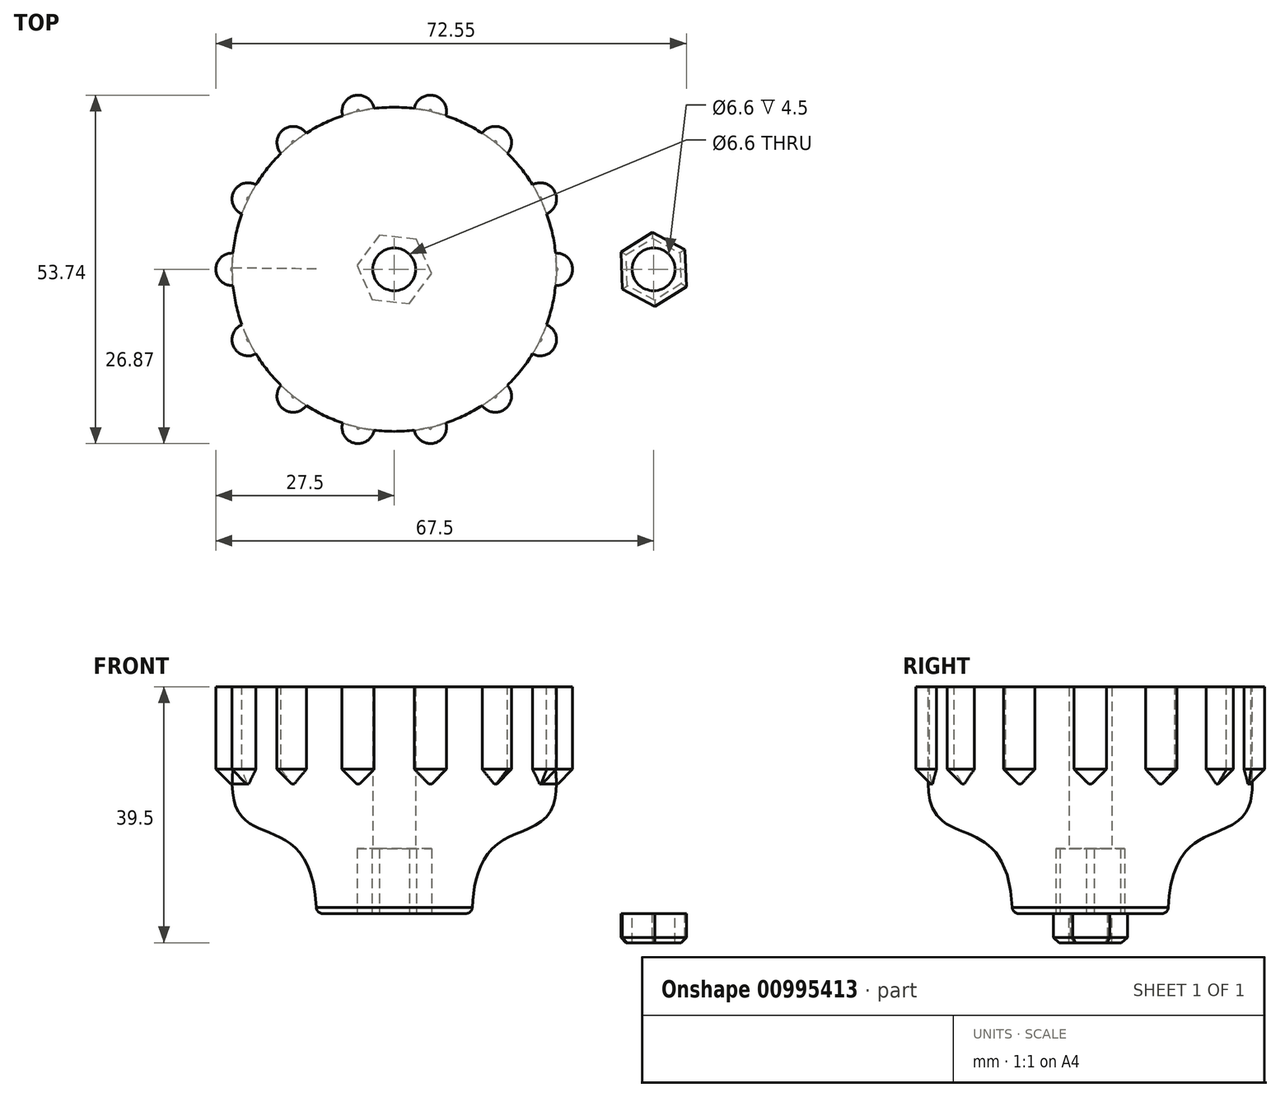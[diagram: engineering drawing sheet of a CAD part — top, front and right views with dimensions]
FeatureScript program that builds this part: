
annotation { "Feature Type Name" : "Feature", "Feature Type Description" : "" }
export const myFeature = defineFeature(function(context is Context, id is Id, definition is map)
    precondition{}
    {
        {
            var Q0;
            Q0=qCreatedBy(makeId("Front.planeOp"),FACE);
            var sketch = newSketch(context, id + "F0", { "sketchPlane" : qUnion([Q0])});
            skLineSegment(sketch, "E0", {"start": v(0, 60.16) * mm, "end": v(0, -58.96) * mm, "construction": true});
            skLineSegment(sketch, "E1", {"start": v(0, -19.71) * mm, "end": v(-12, -19.71) * mm});
            skLineSegment(sketch, "E2", {"start": v(0, 15.29) * mm, "end": v(-25, 15.29) * mm});
            skLineSegment(sketch, "E3", {"start": v(-25, 15.29) * mm, "end": v(-25, 0.29) * mm});
            skFitSpline(sketch, "E4", {"points": [v(-25, 0.29) * mm, v(-12, -19.71) * mm], "startDerivative": vector(0, -34.44) * mm, "endDerivative": vector(1.05, -52.25) * mm});
            skLineSegment(sketch, "E5", {"start": v(0, -19.71) * mm, "end": v(0, 15.29) * mm});
            skSolve(sketch);
        }
        {
            var Q0;
            Q0 = qSketchRegion(id + "F0", true);
            var Q1;
            Q1=sQuery(id+"F0.wireOp",EDGE,"E0");
            revolve(context, id + "F1", {"surfaceOperationType" : NewSurfaceOperationType.NEW, "entities" : qUnion([Q0]), "axis" : qUnion([Q1]), "revolveType" : RevolveType.FULL});
        }
        {
            var Q0;
            Q0=makeQuery(id+"F1.opRevolve","SWEPT_FACE",FACE,{"disambiguationData":[OSD([sQuery(id+"F0.wireOp",EDGE,"E1")])]});
            var sketch = newSketch(context, id + "F2", { "sketchPlane" : qUnion([Q0])});
            skCircle(sketch, "E6", {"center": v(0, 0) * mm, "radius": 3.3 * mm});
            skSolve(sketch);
        }
        {
            var Q0;
            Q0 = qSketchRegion(id + "F2", true);
            extrude(context, id + "F3", {"entities" : qUnion([Q0]), "operationType" : NewBodyOperationType.REMOVE, "endBound" : BoundingType.UP_TO_NEXT, "oppositeDirection" : true, "depth" : 25 * mm, "offsetDistance" : 25 * mm});
        }
        {
            var Q0;
            Q0=makeQuery(id+"F1.opRevolve","SWEPT_FACE",FACE,{"disambiguationData":[OSD([sQuery(id+"F0.wireOp",EDGE,"E1")])]});
            var sketch = newSketch(context, id + "F4", { "sketchPlane" : qUnion([Q0])});
            skCircle(sketch, "E7.cCircle", {"center": v(0, 0) * mm, "radius": 5 * mm, "construction": true});
            skLineSegment(sketch, "E7.0", {"start": v(5.74, 0.63) * mm, "end": v(3.42, -4.65) * mm});
            skLineSegment(sketch, "E7.1", {"start": v(3.42, -4.65) * mm, "end": v(-2.32, -5.29) * mm});
            skLineSegment(sketch, "E7.2", {"start": v(-2.32, -5.29) * mm, "end": v(-5.74, -0.63) * mm});
            skLineSegment(sketch, "E7.3", {"start": v(-5.74, -0.63) * mm, "end": v(-3.42, 4.65) * mm});
            skLineSegment(sketch, "E7.4", {"start": v(-3.42, 4.65) * mm, "end": v(2.32, 5.29) * mm});
            skLineSegment(sketch, "E7.5", {"start": v(2.32, 5.29) * mm, "end": v(5.74, 0.63) * mm});
            skPoint(sketch, "E7.0.midPoint", {"position": v(4.58, -2.01) * mm});
            skSolve(sketch);
        }
        {
            var Q0;
            Q0 = qSketchRegion(id + "F4", true);
            extrude(context, id + "F5", {"entities" : qUnion([Q0]), "operationType" : NewBodyOperationType.REMOVE, "oppositeDirection" : true, "depth" : 10 * mm, "offsetDistance" : 25 * mm});
        }
        {
            var Q0;
            Q0=makeQuery(id+"F1.opRevolve","SWEPT_FACE",FACE,{"disambiguationData":[OSD([sQuery(id+"F0.wireOp",EDGE,"E2")])]});
            var sketch = newSketch(context, id + "F6", { "sketchPlane" : qUnion([Q0])});
            skArc(sketch, "E8", {"start": v(-24.87, 2.5) * mm, "mid": v(-27.5, 0) * mm, "end": v(-24.88, -2.5) * mm});
            skArc(sketch, "E9", {"start": v(-24.88, 2.5) * mm, "mid": v(-25, 0) * mm, "end": v(-24.88, -2.5) * mm});
            skArc(sketch, "E10.1.0", {"start": v(-23.5, -8.54) * mm, "mid": v(-24.78, -11.93) * mm, "end": v(-21.33, -13.04) * mm});
            skArc(sketch, "E10.1.1", {"start": v(-23.5, -8.54) * mm, "mid": v(-22.52, -10.85) * mm, "end": v(-21.33, -13.04) * mm});
            skArc(sketch, "E10.2.0", {"start": v(-17.46, -17.9) * mm, "mid": v(-17.15, -21.5) * mm, "end": v(-13.56, -21) * mm});
            skArc(sketch, "E10.2.1", {"start": v(-17.46, -17.9) * mm, "mid": v(-15.59, -19.55) * mm, "end": v(-13.56, -21) * mm});
            skArc(sketch, "E10.3.0", {"start": v(-7.97, -23.7) * mm, "mid": v(-6.12, -26.81) * mm, "end": v(-3.1, -24.8) * mm});
            skArc(sketch, "E10.3.1", {"start": v(-7.97, -23.7) * mm, "mid": v(-5.56, -24.37) * mm, "end": v(-3.1, -24.8) * mm});
            skArc(sketch, "E10.4.0", {"start": v(3.1, -24.8) * mm, "mid": v(6.12, -26.81) * mm, "end": v(7.97, -23.7) * mm});
            skArc(sketch, "E10.4.1", {"start": v(3.1, -24.8) * mm, "mid": v(5.56, -24.37) * mm, "end": v(7.97, -23.7) * mm});
            skArc(sketch, "E10.5.0", {"start": v(13.56, -21) * mm, "mid": v(17.15, -21.5) * mm, "end": v(17.46, -17.9) * mm});
            skArc(sketch, "E10.5.1", {"start": v(13.56, -21) * mm, "mid": v(15.59, -19.55) * mm, "end": v(17.46, -17.9) * mm});
            skArc(sketch, "E10.6.0", {"start": v(21.33, -13.04) * mm, "mid": v(24.78, -11.93) * mm, "end": v(23.5, -8.54) * mm});
            skArc(sketch, "E10.6.1", {"start": v(21.33, -13.04) * mm, "mid": v(22.52, -10.85) * mm, "end": v(23.5, -8.54) * mm});
            skArc(sketch, "E10.7.0", {"start": v(24.87, -2.5) * mm, "mid": v(27.5, 0) * mm, "end": v(24.88, 2.5) * mm});
            skArc(sketch, "E10.7.1", {"start": v(24.88, -2.5) * mm, "mid": v(25, 0) * mm, "end": v(24.88, 2.5) * mm});
            skArc(sketch, "E10.8.0", {"start": v(23.5, 8.54) * mm, "mid": v(24.78, 11.93) * mm, "end": v(21.33, 13.04) * mm});
            skArc(sketch, "E10.8.1", {"start": v(23.5, 8.54) * mm, "mid": v(22.52, 10.85) * mm, "end": v(21.33, 13.04) * mm});
            skArc(sketch, "E10.9.0", {"start": v(17.46, 17.9) * mm, "mid": v(17.15, 21.5) * mm, "end": v(13.56, 21) * mm});
            skArc(sketch, "E10.9.1", {"start": v(17.46, 17.9) * mm, "mid": v(15.59, 19.55) * mm, "end": v(13.56, 21) * mm});
            skArc(sketch, "E10.10.0", {"start": v(7.97, 23.7) * mm, "mid": v(6.12, 26.81) * mm, "end": v(3.1, 24.8) * mm});
            skArc(sketch, "E10.10.1", {"start": v(7.97, 23.7) * mm, "mid": v(5.56, 24.37) * mm, "end": v(3.1, 24.8) * mm});
            skArc(sketch, "E10.11.0", {"start": v(-3.1, 24.8) * mm, "mid": v(-6.12, 26.81) * mm, "end": v(-7.97, 23.7) * mm});
            skArc(sketch, "E10.11.1", {"start": v(-3.1, 24.8) * mm, "mid": v(-5.56, 24.37) * mm, "end": v(-7.97, 23.7) * mm});
            skArc(sketch, "E10.12.0", {"start": v(-13.56, 21) * mm, "mid": v(-17.15, 21.5) * mm, "end": v(-17.46, 17.9) * mm});
            skArc(sketch, "E10.12.1", {"start": v(-13.56, 21) * mm, "mid": v(-15.59, 19.55) * mm, "end": v(-17.46, 17.9) * mm});
            skArc(sketch, "E10.13.0", {"start": v(-21.33, 13.04) * mm, "mid": v(-24.78, 11.93) * mm, "end": v(-23.5, 8.54) * mm});
            skArc(sketch, "E10.13.1", {"start": v(-21.33, 13.04) * mm, "mid": v(-22.52, 10.85) * mm, "end": v(-23.5, 8.54) * mm});
            skSolve(sketch);
        }
        {
            var Q0;
            Q0 = qSketchRegion(id + "F6", true);
            extrude(context, id + "F7", {"entities" : qUnion([Q0]), "operationType" : NewBodyOperationType.ADD, "oppositeDirection" : true, "depth" : 15 * mm, "offsetDistance" : 25 * mm});
        }
        {
            var Q0;
            Q0=makeQuery(id+"F7.opExtrude","CAP_EDGE",EDGE,{"disambiguationData":[OSD([sQuery(id+"F6.wireOp",EDGE,"E8")])],"isStart":false});
            var Q1;
            Q1=makeQuery(id+"F7.opExtrude","CAP_EDGE",EDGE,{"disambiguationData":[OSD([sQuery(id+"F6.wireOp",EDGE,"E10.13.0")])],"isStart":false});
            var Q2;
            Q2=makeQuery(id+"F7.opExtrude","CAP_EDGE",EDGE,{"disambiguationData":[OSD([sQuery(id+"F6.wireOp",EDGE,"E10.12.0")])],"isStart":false});
            var Q3;
            Q3=makeQuery(id+"F7.opExtrude","CAP_EDGE",EDGE,{"disambiguationData":[OSD([sQuery(id+"F6.wireOp",EDGE,"E10.11.0")])],"isStart":false});
            var Q4;
            Q4=makeQuery(id+"F7.opExtrude","CAP_EDGE",EDGE,{"disambiguationData":[OSD([sQuery(id+"F6.wireOp",EDGE,"E10.10.0")])],"isStart":false});
            var Q5;
            Q5=makeQuery(id+"F7.opExtrude","CAP_EDGE",EDGE,{"disambiguationData":[OSD([sQuery(id+"F6.wireOp",EDGE,"E10.9.0")])],"isStart":false});
            var Q6;
            Q6=makeQuery(id+"F7.opExtrude","CAP_EDGE",EDGE,{"disambiguationData":[OSD([sQuery(id+"F6.wireOp",EDGE,"E10.8.0")])],"isStart":false});
            var Q7;
            Q7=makeQuery(id+"F7.opExtrude","CAP_EDGE",EDGE,{"disambiguationData":[OSD([sQuery(id+"F6.wireOp",EDGE,"E10.7.0")])],"isStart":false});
            var Q8;
            Q8=makeQuery(id+"F7.opExtrude","CAP_EDGE",EDGE,{"disambiguationData":[OSD([sQuery(id+"F6.wireOp",EDGE,"E10.6.0")])],"isStart":false});
            var Q9;
            Q9=makeQuery(id+"F7.opExtrude","CAP_EDGE",EDGE,{"disambiguationData":[OSD([sQuery(id+"F6.wireOp",EDGE,"E10.5.0")])],"isStart":false});
            var Q10;
            Q10=makeQuery(id+"F7.opExtrude","CAP_EDGE",EDGE,{"disambiguationData":[OSD([sQuery(id+"F6.wireOp",EDGE,"E10.4.0")])],"isStart":false});
            var Q11;
            Q11=makeQuery(id+"F7.opExtrude","CAP_EDGE",EDGE,{"disambiguationData":[OSD([sQuery(id+"F6.wireOp",EDGE,"E10.3.0")])],"isStart":false});
            var Q12;
            Q12=makeQuery(id+"F7.opExtrude","CAP_EDGE",EDGE,{"disambiguationData":[OSD([sQuery(id+"F6.wireOp",EDGE,"E10.2.0")])],"isStart":false});
            var Q13;
            Q13=makeQuery(id+"F7.opExtrude","CAP_EDGE",EDGE,{"disambiguationData":[OSD([sQuery(id+"F6.wireOp",EDGE,"E10.1.0")])],"isStart":false});
            chamfer(context, id + "F8", {"entities" : qUnion([Q0, Q1, Q2, Q3, Q4, Q5, Q6, Q7, Q8, Q9, Q10, Q11, Q12, Q13]), "width" : 2.25 * mm, "tangentPropagation" : true});
        }
        {
            var Q0;
            Q0=makeQuery(id+"F1.opRevolve","SWEPT_EDGE",EDGE,{"disambiguationData":[OSD([sQuery(id+"F0.wireOp",EDGE,"E1"),sQuery(id+"F0.wireOp",EDGE,"E4")])]});
            fillet(context, id + "F9", {"entities" : qUnion([Q0]), "radius" : 1 * mm, "tangentPropagation" : true, "allowEdgeOverflow" : false});
        }
        {
            var Q0;
            Q0=makeQuery(id+"F1.opRevolve","SWEPT_FACE",FACE,{"disambiguationData":[OSD([sQuery(id+"F0.wireOp",EDGE,"E1")])]});
            var sketch = newSketch(context, id + "F10", { "sketchPlane" : qUnion([Q0])});
            skCircle(sketch, "E11.cCircle", {"center": v(40, 0) * mm, "radius": 4.95 * mm, "construction": true});
            skLineSegment(sketch, "E11.0", {"start": v(35.15, 3.03) * mm, "end": v(40.2, 5.71) * mm});
            skLineSegment(sketch, "E11.1", {"start": v(40.2, 5.71) * mm, "end": v(45.05, 2.68) * mm});
            skLineSegment(sketch, "E11.2", {"start": v(45.05, 2.68) * mm, "end": v(44.85, -3.03) * mm});
            skLineSegment(sketch, "E11.3", {"start": v(44.85, -3.03) * mm, "end": v(39.8, -5.71) * mm});
            skLineSegment(sketch, "E11.4", {"start": v(39.8, -5.71) * mm, "end": v(34.95, -2.68) * mm});
            skLineSegment(sketch, "E11.5", {"start": v(34.95, -2.68) * mm, "end": v(35.15, 3.03) * mm});
            skPoint(sketch, "E11.0.midPoint", {"position": v(37.68, 4.37) * mm});
            skCircle(sketch, "E12", {"center": v(40, 0) * mm, "radius": 3.3 * mm});
            skSolve(sketch);
        }
        {
            var Q0;
            Q0 = qSketchRegion(id + "F10", true);
            extrude(context, id + "F11", {"entities" : qUnion([Q0]), "depth" : 4.5 * mm, "offsetDistance" : 25 * mm});
        }
        {
            var Q0;
            Q0=makeQuery(id+"F11.opExtrude","CAP_EDGE",EDGE,{"disambiguationData":[OSD([sQuery(id+"F10.wireOp",EDGE,"E11.1")])],"isStart":false});
            var Q1;
            Q1=makeQuery(id+"F11.opExtrude","CAP_EDGE",EDGE,{"disambiguationData":[OSD([sQuery(id+"F10.wireOp",EDGE,"E11.2")])],"isStart":false});
            var Q2;
            Q2=makeQuery(id+"F11.opExtrude","CAP_EDGE",EDGE,{"disambiguationData":[OSD([sQuery(id+"F10.wireOp",EDGE,"E11.3")])],"isStart":false});
            var Q3;
            Q3=makeQuery(id+"F11.opExtrude","CAP_EDGE",EDGE,{"disambiguationData":[OSD([sQuery(id+"F10.wireOp",EDGE,"E11.4")])],"isStart":false});
            var Q4;
            Q4=makeQuery(id+"F11.opExtrude","CAP_EDGE",EDGE,{"disambiguationData":[OSD([sQuery(id+"F10.wireOp",EDGE,"E11.5")])],"isStart":false});
            var Q5;
            Q5=makeQuery(id+"F11.opExtrude","CAP_EDGE",EDGE,{"disambiguationData":[OSD([sQuery(id+"F10.wireOp",EDGE,"E11.0")])],"isStart":false});
            chamfer(context, id + "F12", {"entities" : qUnion([Q0, Q1, Q2, Q3, Q4, Q5]), "width" : 0.8 * mm, "tangentPropagation" : true});
        }
    });
